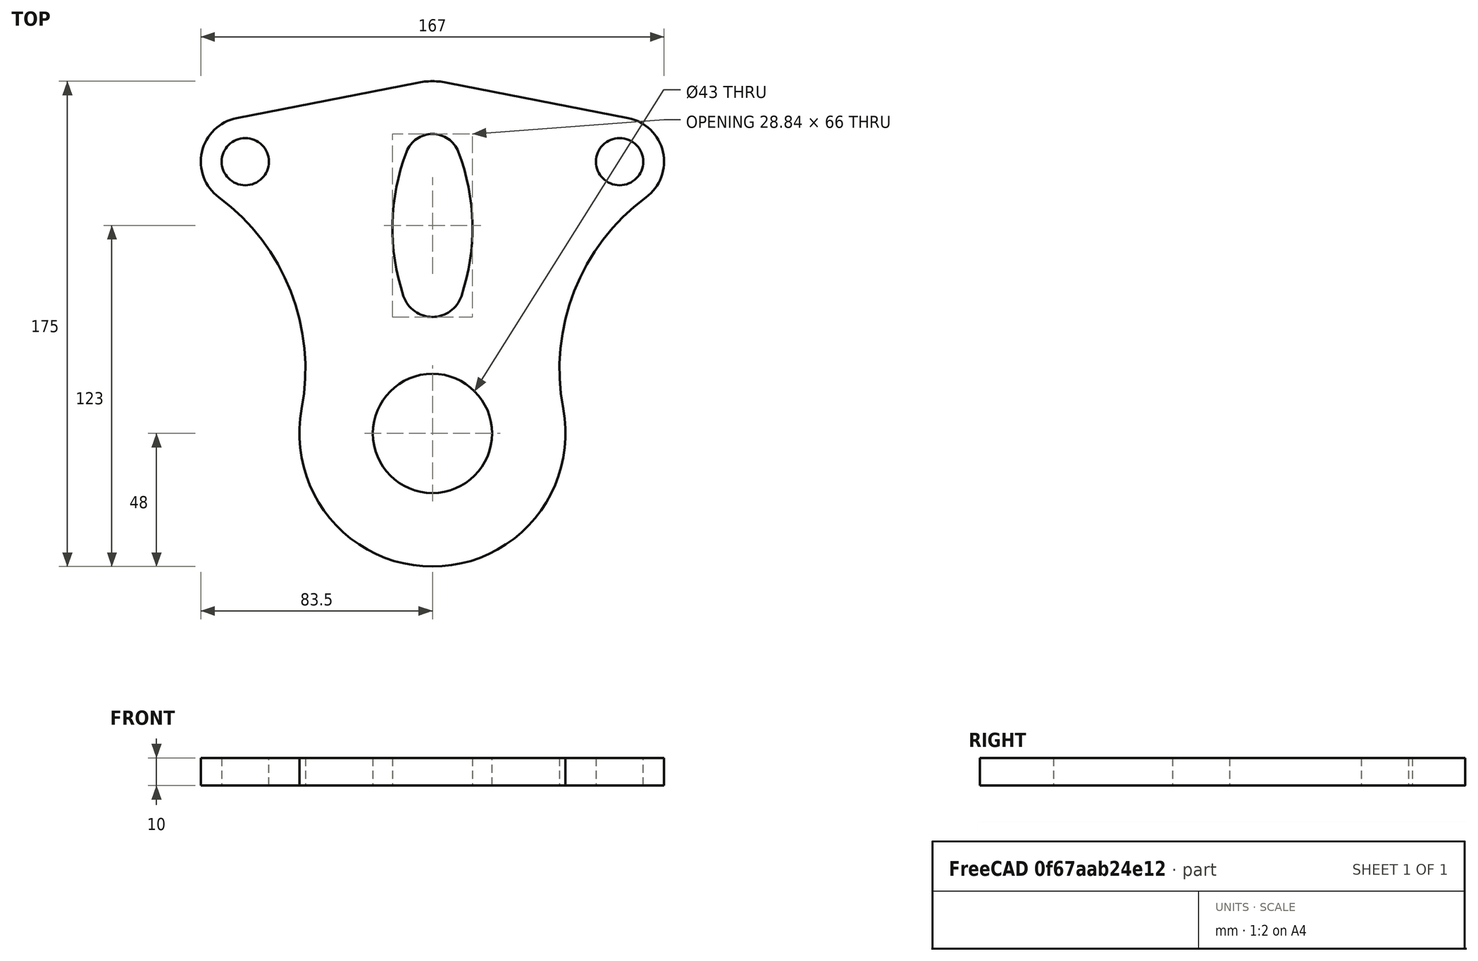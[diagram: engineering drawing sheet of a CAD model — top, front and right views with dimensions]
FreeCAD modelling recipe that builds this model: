
FCSTD DOCUMENT  (FreeCAD 1.0R39109 (Git))
Label: Задание 2-1
License: All rights reserved
LicenseURL: https://en.wikipedia.org/wiki/All_rights_reserved
objects: Sketcher::SketchObject×1, PartDesign::Pad×1, PartDesign::Body×1
note: 6 computed .brp shape members not serialized (recipe doc carries the construction recipe); baked Part::Feature solids carry a one-line shape summary decoded from their .brp

FEATURE [Sketcher::SketchObject] Sketch
  ArcFitTolerance = 1e-06
  AttachmentSupport = -> [XY_Plane]
  FullyConstrained = true
  MakeInternals = false
  MapMode = 5
  sketch-geometry (16):
    g0: ArcOfCircle CenterX=0 CenterY=0 CenterZ=0 NormalX=0 NormalY=0 NormalZ=1 AngleXU=0 Radius=10 StartAngle=0.365994 EndAngle=2.7756
    g1: Circle CenterX=-67.5 CenterY=0 CenterZ=0 NormalX=0 NormalY=0 NormalZ=1 AngleXU=0 Radius=8.5
    g2: Circle CenterX=67.5 CenterY=0 CenterZ=0 NormalX=0 NormalY=0 NormalZ=1 AngleXU=0 Radius=8.5
    g3: Circle CenterX=0 CenterY=-98 CenterZ=0 NormalX=0 NormalY=0 NormalZ=1 AngleXU=0 Radius=21.5
    g4: ArcOfCircle CenterX=0 CenterY=-98 CenterZ=0 NormalX=0 NormalY=0 NormalZ=1 AngleXU=0 Radius=48 StartAngle=2.95456 EndAngle=6.47021
    g5: ArcOfCircle CenterX=-122.82 CenterY=-74.7575 CenterZ=0 NormalX=0 NormalY=0 NormalZ=1 AngleXU=0 Radius=77 StartAngle=6.09616 EndAngle=7.21691
    g6: ArcOfCircle CenterX=122.82 CenterY=-74.7575 CenterZ=0 NormalX=0 NormalY=0 NormalZ=1 AngleXU=0 Radius=77 StartAngle=2.20786 EndAngle=3.32862
    g7: ArcOfCircle CenterX=0 CenterY=-45 CenterZ=0 NormalX=0 NormalY=0 NormalZ=1 AngleXU=0 Radius=11 StartAngle=3.46576 EndAngle=5.95902
    g8: ArcOfCircle CenterX=-62.5625 CenterY=-23.9778 CenterZ=0 NormalX=0 NormalY=0 NormalZ=1 AngleXU=0 Radius=77 StartAngle=5.95902 EndAngle=6.64918
    g9: ArcOfCircle CenterX=62.5625 CenterY=-23.9778 CenterZ=0 NormalX=0 NormalY=0 NormalZ=1 AngleXU=0 Radius=77 StartAngle=2.7756 EndAngle=3.46576
    g10: ArcOfCircle CenterX=-67.5 CenterY=0 CenterZ=0 NormalX=0 NormalY=0 NormalZ=1 AngleXU=0 Radius=16 StartAngle=1.7646 EndAngle=4.07532
    g11: ArcOfCircle CenterX=67.5 CenterY=0 CenterZ=0 NormalX=0 NormalY=0 NormalZ=1 AngleXU=0 Radius=16 StartAngle=5.34946 EndAngle=7.66018
    g12: LineSegment StartX=-5.58519 StartY=28.4571 StartZ=0 EndX=-70.5815 EndY=15.7005 EndZ=0
    g13: LineSegment StartX=5.58519 StartY=28.4571 StartZ=0 EndX=70.5815 EndY=15.7005 EndZ=0
    g14: ArcOfCircle CenterX=1.25e-14 CenterY=0 CenterZ=0 NormalX=0 NormalY=0 NormalZ=1 AngleXU=0 Radius=29 StartAngle=1.37699 EndAngle=1.7646
    g15: GeomPoint [constr] X=0 Y=29.5533 Z=0
  constraints (41):
    c: Diameter(g0) = 20
    c: Coincident(g0,g-1)
    c: Diameter(g1) = 17
    c: PointOnObject(g1,g-1)
    c: Diameter(g2) = 17
    c: PointOnObject(g2,g-1)
    c: DistanceX(g0,g2) = 67.5
    c: Diameter(g3) = 43
    c: PointOnObject(g3,g-2)
    c: Diameter(g4) = 96
    c: Coincident(g4,g3)
    c: Radius(g6) = 77
    c: Radius(g5) = 77
    c: Tangent(g4,g6) = 1.5708
    c: Tangent(g4,g5) = 1.5708
    c: DistanceY(g3,g0) = 98
    c: Diameter(g7) = 22
    c: PointOnObject(g7,g-2)
    c: DistanceY(g7,g0) = 45
    c: Radius(g8) = 77
    c: Radius(g9) = 77
    c: Tangent(g0,g9) = -1.5708
    c: Tangent(g0,g8) = -1.5708
    c: Tangent(g7,g8) = -1.5708
    c: Tangent(g7,g9) = -1.5708
    c: DistanceX(g1,g0) = 67.5
    c: Diameter(g10) = 32
    c: Coincident(g10,g1)
    c: Diameter(g11) = 32
    c: Coincident(g11,g2)
    c: PointOnObject(g15,g-2)
    c: PointOnObject(g15,g12)
    c: PointOnObject(g15,g13)
    c: Tangent(g12,g14) = -1.5708
    c: Tangent(g13,g14) = 1.5708
    c: Diameter(g14) = 58
    c: PointOnObject(g14,g-1)
    c: Tangent(g11,g13) = 1.5708
    c: Tangent(g10,g12) = -1.5708
    c: Tangent(g5,g10) = 1.5708
    c: Tangent(g11,g6) = 1.5708
FEATURE [PartDesign::Pad] Pad
  Direction = (0,0,1)
  Length = 10
  Length2 = 10
  Profile = -> Sketch
  ReferenceAxis = -> Sketch [N_Axis]
  Refine = true
  Suppressed = false
  Type = 0
FEATURE [PartDesign::Body] Body
  AllowCompound = false
  Group = -> [Sketch,Pad]
  Origin = -> Origin
  Tip = -> Pad
